# Revit family: CD1000FT
name_source: partatom
category: Mechanical Equipment
revit_build: Autodesk Revit 2017 (Build: 20160225_1515(x64)
units: mm (PartAtom-declared; Revit-internal decimal feet)

## family parameters
Always vertical = Yes
Cut with Voids When Loaded = No
OmniClass Number = 23.65.35.11.17
OmniClass Title = Thermodynamic Water Heaters
Part Type = Normal
Room Calculation Point = No
Round Connector Dimension = Use Diameter
Shared = No
Work Plane-Based = No

## types (1)
- CD1000FT
    Anchorage = 0.625" holes for 0.5" anchors x4)
    Boiler Condensate Drain = 0.75" hose barb tubing
    Boiler Natural Gas Supply = 1.00" NPT  4" to 13" W.C.
    Boiler Vent = 4" CAT IV
    Cold Water Make Up = 0.75" NPT
    Description = Flowtherm Hydronic Heating Module (HHM)
    Expansion Tank/Air Separator Drain = 0.75" NPT
    FLA = 11.4@460V / 21.8@230V / 24.0@208V
    Flow Rate = 65 GPM
    Hot Water Return = 2.50" - 150# Flange
    Hot Water Supply = 2.50" - 150# Flange
    Input Rate = 1000 MBH
    Manufacturer = FlowTherm Systems
    Model = CD1000FT
    Output Rate = 978 MBH
    Phase = 3
    Pot Feeder Drain = 0.50" NPT
    System Integration Panel (SIP) = NEMA 1/3R enclosure, non-fused main power disconnect
    Total Dynamic Head = 65'
    URL = www.FLOWTHERM.com
    Weight (pounds) = 3980

## geometry (parser evidence)
native form markers: Sweep x2
no freeform markers — native parametric forms only
